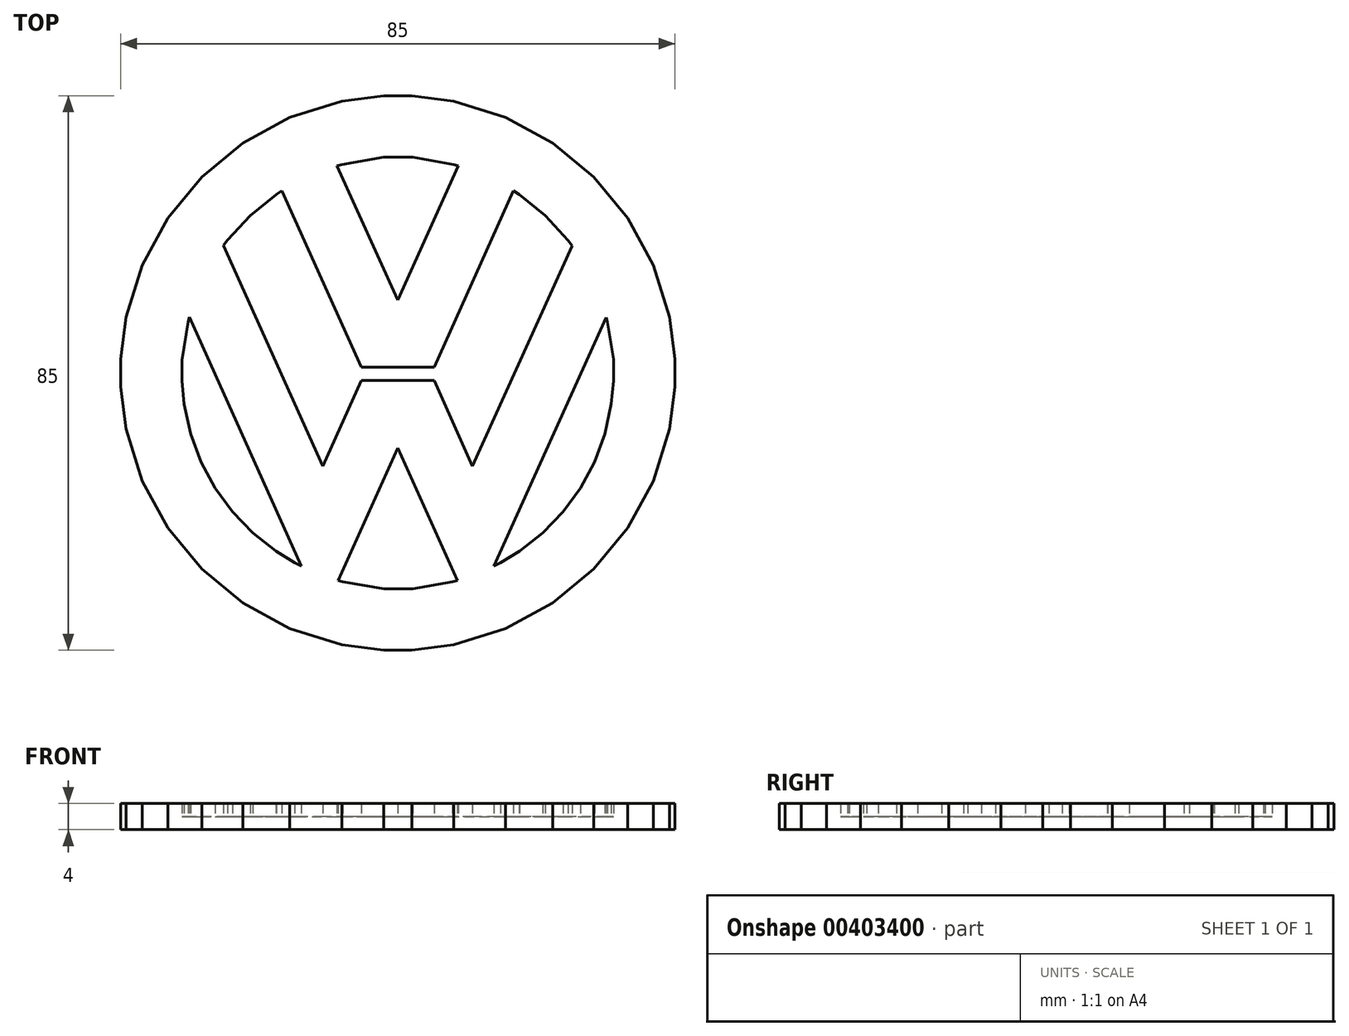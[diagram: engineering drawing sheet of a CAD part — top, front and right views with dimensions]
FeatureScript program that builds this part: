
annotation { "Feature Type Name" : "Feature", "Feature Type Description" : "" }
export const myFeature = defineFeature(function(context is Context, id is Id, definition is map)
    precondition{}
    {
        {
            var Q0;
            Q0=qCreatedBy(makeId("Top.planeOp"),FACE);
            var sketch = newSketch(context, id + "F0", { "sketchPlane" : qUnion([Q0])});
            skLineSegment(sketch, "E0", {"start": v(-0.01, 46.67) * mm, "end": v(-2.37, 46.67) * mm});
            skLineSegment(sketch, "E1", {"start": v(-2.37, 46.67) * mm, "end": v(-9.42, 45.73) * mm});
            skLineSegment(sketch, "E2", {"start": v(-9.42, 45.73) * mm, "end": v(-18.19, 43) * mm});
            skLineSegment(sketch, "E3", {"start": v(-18.19, 43) * mm, "end": v(-26.12, 38.7) * mm});
            skLineSegment(sketch, "E4", {"start": v(-26.12, 38.7) * mm, "end": v(-33.03, 33) * mm});
            skLineSegment(sketch, "E5", {"start": v(-33.03, 33) * mm, "end": v(-38.73, 26.1) * mm});
            skLineSegment(sketch, "E6", {"start": v(-38.73, 26.1) * mm, "end": v(-43.03, 18.16) * mm});
            skLineSegment(sketch, "E7", {"start": v(-43.03, 18.16) * mm, "end": v(-45.75, 9.4) * mm});
            skLineSegment(sketch, "E8", {"start": v(-45.75, 9.4) * mm, "end": v(-46.7, 2.34) * mm});
            skLineSegment(sketch, "E9", {"start": v(-46.7, 2.34) * mm, "end": v(-46.7, -0.01) * mm});
            skLineSegment(sketch, "E10", {"start": v(-46.7, -0.01) * mm, "end": v(-46.7, -2.36) * mm});
            skLineSegment(sketch, "E11", {"start": v(-46.7, -2.36) * mm, "end": v(-45.75, -9.42) * mm});
            skLineSegment(sketch, "E12", {"start": v(-45.75, -9.42) * mm, "end": v(-43.03, -18.18) * mm});
            skLineSegment(sketch, "E13", {"start": v(-43.03, -18.18) * mm, "end": v(-38.73, -26.11) * mm});
            skLineSegment(sketch, "E14", {"start": v(-38.73, -26.11) * mm, "end": v(-33.03, -33.02) * mm});
            skLineSegment(sketch, "E15", {"start": v(-33.03, -33.02) * mm, "end": v(-26.12, -38.73) * mm});
            skLineSegment(sketch, "E16", {"start": v(-26.12, -38.73) * mm, "end": v(-18.19, -43.03) * mm});
            skLineSegment(sketch, "E17", {"start": v(-18.19, -43.03) * mm, "end": v(-9.42, -45.75) * mm});
            skLineSegment(sketch, "E18", {"start": v(-9.42, -45.75) * mm, "end": v(-2.37, -46.7) * mm});
            skLineSegment(sketch, "E19", {"start": v(-2.37, -46.7) * mm, "end": v(-0.01, -46.7) * mm});
            skLineSegment(sketch, "E20", {"start": v(-0.01, -46.7) * mm, "end": v(2.34, -46.7) * mm});
            skLineSegment(sketch, "E21", {"start": v(2.34, -46.7) * mm, "end": v(9.4, -45.75) * mm});
            skLineSegment(sketch, "E22", {"start": v(9.4, -45.75) * mm, "end": v(18.16, -43.03) * mm});
            skLineSegment(sketch, "E23", {"start": v(18.16, -43.03) * mm, "end": v(26.09, -38.73) * mm});
            skLineSegment(sketch, "E24", {"start": v(26.09, -38.73) * mm, "end": v(33, -33.02) * mm});
            skLineSegment(sketch, "E25", {"start": v(33, -33.02) * mm, "end": v(38.7, -26.11) * mm});
            skLineSegment(sketch, "E26", {"start": v(38.7, -26.11) * mm, "end": v(43, -18.18) * mm});
            skLineSegment(sketch, "E27", {"start": v(43, -18.18) * mm, "end": v(45.72, -9.42) * mm});
            skLineSegment(sketch, "E28", {"start": v(45.72, -9.42) * mm, "end": v(46.67, -2.36) * mm});
            skLineSegment(sketch, "E29", {"start": v(46.67, -2.36) * mm, "end": v(46.67, -0.01) * mm});
            skLineSegment(sketch, "E30", {"start": v(46.67, -0.01) * mm, "end": v(46.67, 2.34) * mm});
            skLineSegment(sketch, "E31", {"start": v(46.67, 2.34) * mm, "end": v(45.72, 9.4) * mm});
            skLineSegment(sketch, "E32", {"start": v(45.72, 9.4) * mm, "end": v(43, 18.16) * mm});
            skLineSegment(sketch, "E33", {"start": v(43, 18.16) * mm, "end": v(38.7, 26.1) * mm});
            skLineSegment(sketch, "E34", {"start": v(38.7, 26.1) * mm, "end": v(33, 33) * mm});
            skLineSegment(sketch, "E35", {"start": v(33, 33) * mm, "end": v(26.09, 38.7) * mm});
            skLineSegment(sketch, "E36", {"start": v(26.09, 38.7) * mm, "end": v(18.16, 43) * mm});
            skLineSegment(sketch, "E37", {"start": v(18.16, 43) * mm, "end": v(9.4, 45.73) * mm});
            skLineSegment(sketch, "E38", {"start": v(9.4, 45.73) * mm, "end": v(2.34, 46.67) * mm});
            skLineSegment(sketch, "E39", {"start": v(2.34, 46.67) * mm, "end": v(-0.01, 46.67) * mm});
            skLineSegment(sketch, "E40", {"start": v(-0.01, -42.51) * mm, "end": v(-2.16, -42.51) * mm});
            skLineSegment(sketch, "E41", {"start": v(-2.16, -42.51) * mm, "end": v(-8.58, -41.65) * mm});
            skLineSegment(sketch, "E42", {"start": v(-8.58, -41.65) * mm, "end": v(-16.56, -39.17) * mm});
            skLineSegment(sketch, "E43", {"start": v(-16.56, -39.17) * mm, "end": v(-23.78, -35.25) * mm});
            skLineSegment(sketch, "E44", {"start": v(-23.78, -35.25) * mm, "end": v(-30.06, -30.06) * mm});
            skLineSegment(sketch, "E45", {"start": v(-30.06, -30.06) * mm, "end": v(-35.25, -23.77) * mm});
            skLineSegment(sketch, "E46", {"start": v(-35.25, -23.77) * mm, "end": v(-39.17, -16.55) * mm});
            skLineSegment(sketch, "E47", {"start": v(-39.17, -16.55) * mm, "end": v(-41.65, -8.58) * mm});
            skLineSegment(sketch, "E48", {"start": v(-41.65, -8.58) * mm, "end": v(-42.51, -2.15) * mm});
            skLineSegment(sketch, "E49", {"start": v(-42.51, -2.15) * mm, "end": v(-42.51, -0.01) * mm});
            skLineSegment(sketch, "E50", {"start": v(-42.51, -0.01) * mm, "end": v(-42.51, 2.13) * mm});
            skLineSegment(sketch, "E51", {"start": v(-42.51, 2.13) * mm, "end": v(-41.65, 8.55) * mm});
            skLineSegment(sketch, "E52", {"start": v(-41.65, 8.55) * mm, "end": v(-39.17, 16.53) * mm});
            skLineSegment(sketch, "E53", {"start": v(-39.17, 16.53) * mm, "end": v(-35.25, 23.75) * mm});
            skLineSegment(sketch, "E54", {"start": v(-35.25, 23.75) * mm, "end": v(-30.06, 30.04) * mm});
            skLineSegment(sketch, "E55", {"start": v(-30.06, 30.04) * mm, "end": v(-23.78, 35.23) * mm});
            skLineSegment(sketch, "E56", {"start": v(-23.78, 35.23) * mm, "end": v(-16.56, 39.15) * mm});
            skLineSegment(sketch, "E57", {"start": v(-16.56, 39.15) * mm, "end": v(-8.58, 41.63) * mm});
            skLineSegment(sketch, "E58", {"start": v(-8.58, 41.63) * mm, "end": v(-2.16, 42.49) * mm});
            skLineSegment(sketch, "E59", {"start": v(-2.16, 42.49) * mm, "end": v(-0.01, 42.49) * mm});
            skLineSegment(sketch, "E60", {"start": v(-0.01, 42.49) * mm, "end": v(2.13, 42.49) * mm});
            skLineSegment(sketch, "E61", {"start": v(2.13, 42.49) * mm, "end": v(8.55, 41.63) * mm});
            skLineSegment(sketch, "E62", {"start": v(8.55, 41.63) * mm, "end": v(16.53, 39.15) * mm});
            skLineSegment(sketch, "E63", {"start": v(16.53, 39.15) * mm, "end": v(23.75, 35.23) * mm});
            skLineSegment(sketch, "E64", {"start": v(23.75, 35.23) * mm, "end": v(30.04, 30.04) * mm});
            skLineSegment(sketch, "E65", {"start": v(30.04, 30.04) * mm, "end": v(35.23, 23.75) * mm});
            skLineSegment(sketch, "E66", {"start": v(35.23, 23.75) * mm, "end": v(39.15, 16.53) * mm});
            skLineSegment(sketch, "E67", {"start": v(39.15, 16.53) * mm, "end": v(41.62, 8.55) * mm});
            skLineSegment(sketch, "E68", {"start": v(41.62, 8.55) * mm, "end": v(42.49, 2.13) * mm});
            skLineSegment(sketch, "E69", {"start": v(42.49, 2.13) * mm, "end": v(42.49, -0.01) * mm});
            skLineSegment(sketch, "E70", {"start": v(42.49, -0.01) * mm, "end": v(42.49, -2.15) * mm});
            skLineSegment(sketch, "E71", {"start": v(42.49, -2.15) * mm, "end": v(41.62, -8.58) * mm});
            skLineSegment(sketch, "E72", {"start": v(41.62, -8.58) * mm, "end": v(39.15, -16.55) * mm});
            skLineSegment(sketch, "E73", {"start": v(39.15, -16.55) * mm, "end": v(35.23, -23.77) * mm});
            skLineSegment(sketch, "E74", {"start": v(35.23, -23.77) * mm, "end": v(30.04, -30.06) * mm});
            skLineSegment(sketch, "E75", {"start": v(30.04, -30.06) * mm, "end": v(23.75, -35.25) * mm});
            skLineSegment(sketch, "E76", {"start": v(23.75, -35.25) * mm, "end": v(16.53, -39.17) * mm});
            skLineSegment(sketch, "E77", {"start": v(16.53, -39.17) * mm, "end": v(8.55, -41.65) * mm});
            skLineSegment(sketch, "E78", {"start": v(8.55, -41.65) * mm, "end": v(2.13, -42.51) * mm});
            skLineSegment(sketch, "E79", {"start": v(2.13, -42.51) * mm, "end": v(-0.01, -42.51) * mm});
            skLineSegment(sketch, "E80", {"start": v(-9.32, 31.74) * mm, "end": v(-8.58, 31.96) * mm});
            skLineSegment(sketch, "E81", {"start": v(-8.58, 31.96) * mm, "end": v(-2.16, 33.06) * mm});
            skLineSegment(sketch, "E82", {"start": v(-2.16, 33.06) * mm, "end": v(-0.01, 33.06) * mm});
            skLineSegment(sketch, "E83", {"start": v(-0.01, 33.06) * mm, "end": v(2.31, 33.06) * mm});
            skLineSegment(sketch, "E84", {"start": v(2.31, 33.06) * mm, "end": v(8.54, 31.96) * mm});
            skLineSegment(sketch, "E85", {"start": v(8.54, 31.96) * mm, "end": v(9.28, 31.74) * mm});
            skLineSegment(sketch, "E86", {"start": v(9.28, 31.74) * mm, "end": v(-0.01, 11.14) * mm});
            skLineSegment(sketch, "E87", {"start": v(-0.01, 11.14) * mm, "end": v(-9.32, 31.74) * mm});
            skLineSegment(sketch, "E88", {"start": v(17.74, 27.9) * mm, "end": v(18.62, 27.34) * mm});
            skLineSegment(sketch, "E89", {"start": v(18.62, 27.34) * mm, "end": v(22.62, 24.11) * mm});
            skLineSegment(sketch, "E90", {"start": v(22.62, 24.11) * mm, "end": v(26.1, 20.33) * mm});
            skLineSegment(sketch, "E91", {"start": v(26.1, 20.33) * mm, "end": v(26.7, 19.5) * mm});
            skLineSegment(sketch, "E92", {"start": v(26.7, 19.5) * mm, "end": v(11.45, -14.27) * mm});
            skLineSegment(sketch, "E93", {"start": v(11.45, -14.27) * mm, "end": v(5.57, -1.18) * mm});
            skLineSegment(sketch, "E94", {"start": v(5.57, -1.18) * mm, "end": v(-5.6, -1.18) * mm});
            skLineSegment(sketch, "E95", {"start": v(-5.6, -1.18) * mm, "end": v(-11.48, -14.27) * mm});
            skLineSegment(sketch, "E96", {"start": v(-11.48, -14.27) * mm, "end": v(-26.7, 19.52) * mm});
            skLineSegment(sketch, "E97", {"start": v(-26.7, 19.52) * mm, "end": v(-26.1, 20.35) * mm});
            skLineSegment(sketch, "E98", {"start": v(-26.1, 20.35) * mm, "end": v(-22.63, 24.13) * mm});
            skLineSegment(sketch, "E99", {"start": v(-22.63, 24.13) * mm, "end": v(-18.64, 27.35) * mm});
            skLineSegment(sketch, "E100", {"start": v(-18.64, 27.35) * mm, "end": v(-17.77, 27.9) * mm});
            skLineSegment(sketch, "E101", {"start": v(-17.77, 27.9) * mm, "end": v(-5.6, 0.88) * mm});
            skLineSegment(sketch, "E102", {"start": v(-5.6, 0.88) * mm, "end": v(5.6, 0.88) * mm});
            skLineSegment(sketch, "E103", {"start": v(5.6, 0.88) * mm, "end": v(17.74, 27.9) * mm});
            skLineSegment(sketch, "E104", {"start": v(-31.97, 8.55) * mm, "end": v(-32.16, 7.87) * mm});
            skLineSegment(sketch, "E105", {"start": v(-32.16, 7.87) * mm, "end": v(-33.1, 1.96) * mm});
            skLineSegment(sketch, "E106", {"start": v(-33.1, 1.96) * mm, "end": v(-33.1, -0.01) * mm});
            skLineSegment(sketch, "E107", {"start": v(-33.1, -0.01) * mm, "end": v(-33.1, -1.2) * mm});
            skLineSegment(sketch, "E108", {"start": v(-33.1, -1.2) * mm, "end": v(-32.75, -4.78) * mm});
            skLineSegment(sketch, "E109", {"start": v(-32.75, -4.78) * mm, "end": v(-31.76, -9.34) * mm});
            skLineSegment(sketch, "E110", {"start": v(-31.76, -9.34) * mm, "end": v(-30.16, -13.65) * mm});
            skLineSegment(sketch, "E111", {"start": v(-30.16, -13.65) * mm, "end": v(-28, -17.64) * mm});
            skLineSegment(sketch, "E112", {"start": v(-28, -17.64) * mm, "end": v(-25.34, -21.29) * mm});
            skLineSegment(sketch, "E113", {"start": v(-25.34, -21.29) * mm, "end": v(-22.22, -24.53) * mm});
            skLineSegment(sketch, "E114", {"start": v(-22.22, -24.53) * mm, "end": v(-18.68, -27.32) * mm});
            skLineSegment(sketch, "E115", {"start": v(-18.68, -27.32) * mm, "end": v(-15.8, -29.12) * mm});
            skLineSegment(sketch, "E116", {"start": v(-15.8, -29.12) * mm, "end": v(-14.78, -29.62) * mm});
            skLineSegment(sketch, "E117", {"start": v(-14.78, -29.62) * mm, "end": v(-31.97, 8.55) * mm});
            skLineSegment(sketch, "E118", {"start": v(-9.16, -31.81) * mm, "end": v(-8.44, -32.02) * mm});
            skLineSegment(sketch, "E119", {"start": v(-8.44, -32.02) * mm, "end": v(-2.12, -33.1) * mm});
            skLineSegment(sketch, "E120", {"start": v(-2.12, -33.1) * mm, "end": v(-0.01, -33.1) * mm});
            skLineSegment(sketch, "E121", {"start": v(-0.01, -33.1) * mm, "end": v(2.27, -33.1) * mm});
            skLineSegment(sketch, "E122", {"start": v(2.27, -33.1) * mm, "end": v(8.4, -32.02) * mm});
            skLineSegment(sketch, "E123", {"start": v(8.4, -32.02) * mm, "end": v(9.13, -31.81) * mm});
            skLineSegment(sketch, "E124", {"start": v(9.13, -31.81) * mm, "end": v(-0.01, -11.52) * mm});
            skLineSegment(sketch, "E125", {"start": v(-0.01, -11.52) * mm, "end": v(-9.16, -31.81) * mm});
            skLineSegment(sketch, "E126", {"start": v(14.75, -29.62) * mm, "end": v(15.76, -29.12) * mm});
            skLineSegment(sketch, "E127", {"start": v(15.76, -29.12) * mm, "end": v(18.66, -27.32) * mm});
            skLineSegment(sketch, "E128", {"start": v(18.66, -27.32) * mm, "end": v(22.2, -24.53) * mm});
            skLineSegment(sketch, "E129", {"start": v(22.2, -24.53) * mm, "end": v(25.32, -21.29) * mm});
            skLineSegment(sketch, "E130", {"start": v(25.32, -21.29) * mm, "end": v(27.98, -17.64) * mm});
            skLineSegment(sketch, "E131", {"start": v(27.98, -17.64) * mm, "end": v(30.13, -13.65) * mm});
            skLineSegment(sketch, "E132", {"start": v(30.13, -13.65) * mm, "end": v(31.73, -9.34) * mm});
            skLineSegment(sketch, "E133", {"start": v(31.73, -9.34) * mm, "end": v(32.72, -4.78) * mm});
            skLineSegment(sketch, "E134", {"start": v(32.72, -4.78) * mm, "end": v(33.07, -1.2) * mm});
            skLineSegment(sketch, "E135", {"start": v(33.07, -1.2) * mm, "end": v(33.07, -0.01) * mm});
            skLineSegment(sketch, "E136", {"start": v(33.07, -0.01) * mm, "end": v(33.07, 2.11) * mm});
            skLineSegment(sketch, "E137", {"start": v(33.07, 2.11) * mm, "end": v(32.15, 7.8) * mm});
            skLineSegment(sketch, "E138", {"start": v(32.15, 7.8) * mm, "end": v(31.97, 8.48) * mm});
            skLineSegment(sketch, "E139", {"start": v(31.97, 8.48) * mm, "end": v(14.75, -29.62) * mm});
            skSolve(sketch);
        }
        {
            var Q0;
            Q0=makeQuery(id+"F0.imprint","IMPRINT",FACE,{"disambiguationData":[TD([[makeQuery(id+"F0.imprint","IMPRINT",EDGE,{"derivedFrom":sQuery(id+"F0.wireOp",EDGE,"E40")}),-1.0]])]});
            extrude(context, id + "F1", {"entities" : qUnion([Q0]), "depth" : 4 * mm});
        }
        {
            var Q0;
            Q0=makeQuery(id+"F0.imprint","IMPRINT",FACE,{"disambiguationData":[TD([[makeQuery(id+"F0.imprint","IMPRINT",EDGE,{"derivedFrom":sQuery(id+"F0.wireOp",EDGE,"E88")}),-1.0]])]});
            var Q1;
            Q1=makeQuery(id+"F0.imprint","IMPRINT",FACE,{"disambiguationData":[TD([[makeQuery(id+"F0.imprint","IMPRINT",EDGE,{"derivedFrom":sQuery(id+"F0.wireOp",EDGE,"E104")}),1.0]])]});
            var Q2;
            Q2=makeQuery(id+"F0.imprint","IMPRINT",FACE,{"disambiguationData":[TD([[makeQuery(id+"F0.imprint","IMPRINT",EDGE,{"derivedFrom":sQuery(id+"F0.wireOp",EDGE,"E118")}),1.0]])]});
            var Q3;
            Q3=makeQuery(id+"F0.imprint","IMPRINT",FACE,{"disambiguationData":[TD([[makeQuery(id+"F0.imprint","IMPRINT",EDGE,{"derivedFrom":sQuery(id+"F0.wireOp",EDGE,"E126")}),1.0]])]});
            var Q4;
            Q4=makeQuery(id+"F0.imprint","IMPRINT",FACE,{"disambiguationData":[TD([[makeQuery(id+"F0.imprint","IMPRINT",EDGE,{"derivedFrom":sQuery(id+"F0.wireOp",EDGE,"E80")}),-1.0]])]});
            extrude(context, id + "F2", {"entities" : qUnion([Q0, Q1, Q2, Q3, Q4]), "operationType" : NewBodyOperationType.ADD, "depth" : 2 * mm});
        }
    });
